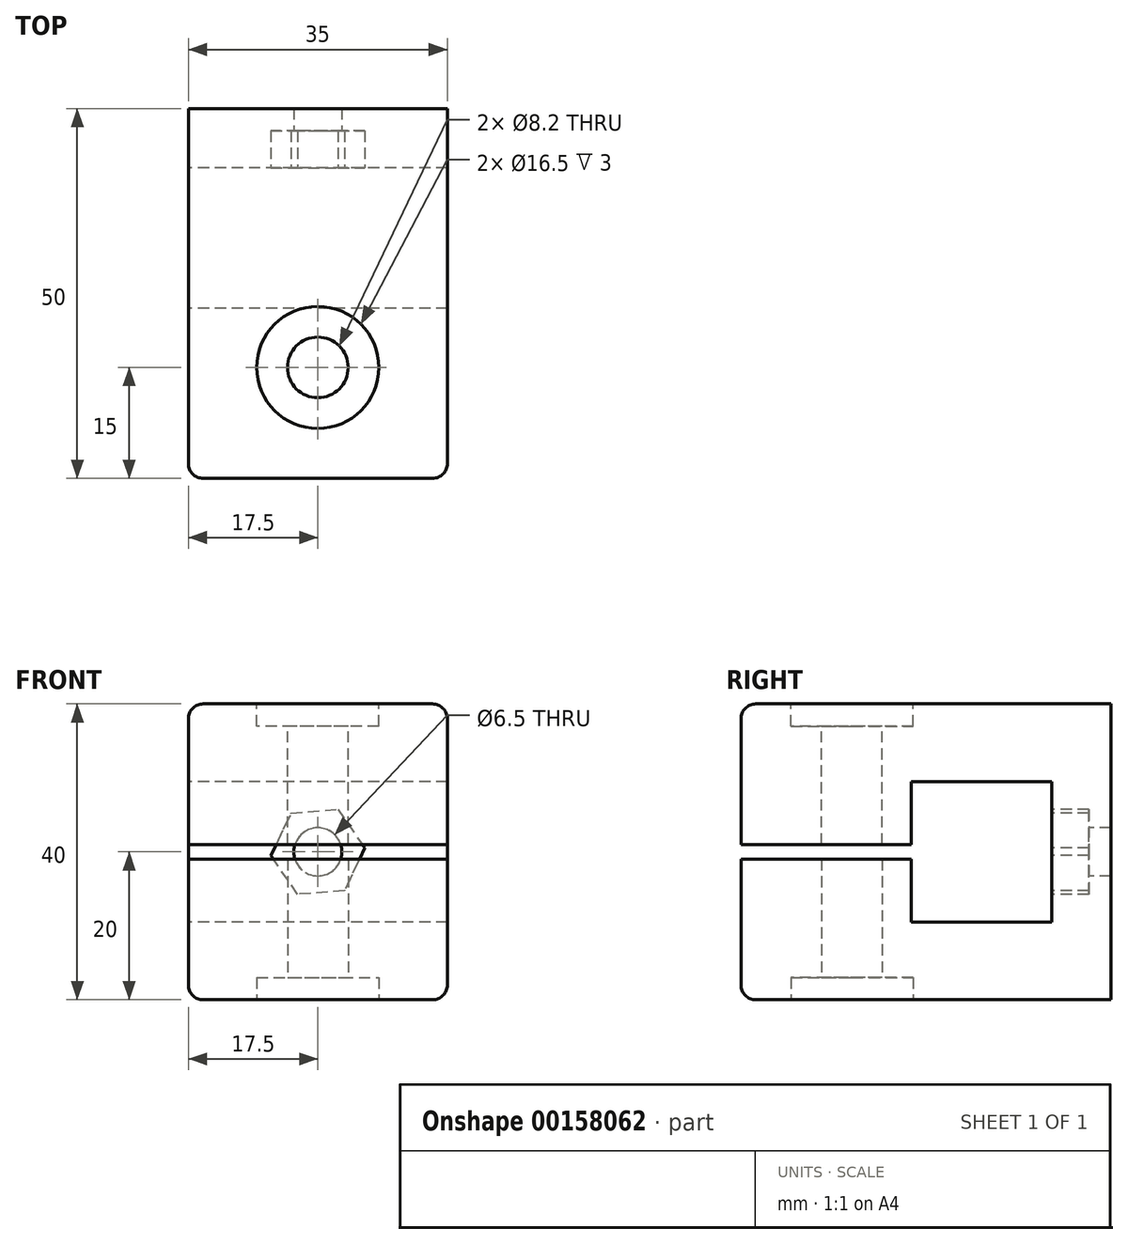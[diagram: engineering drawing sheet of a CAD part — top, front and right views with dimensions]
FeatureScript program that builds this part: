
annotation { "Feature Type Name" : "Feature", "Feature Type Description" : "" }
export const myFeature = defineFeature(function(context is Context, id is Id, definition is map)
    precondition{}
    {
        {
            var Q0;
            Q0=qCreatedBy(makeId("Right.planeOp"),FACE);
            var sketch = newSketch(context, id + "F0", { "sketchPlane" : qUnion([Q0])});
            skLineSegment(sketch, "E0.bottom", {"start": v(9.5, -9.5) * mm, "end": v(-9.5, -9.5) * mm});
            skLineSegment(sketch, "E0.top", {"start": v(9.5, 9.5) * mm, "end": v(-9.5, 9.5) * mm});
            skLineSegment(sketch, "E0.left", {"start": v(9.5, -9.5) * mm, "end": v(9.5, 9.5) * mm});
            skLineSegment(sketch, "E0.right", {"start": v(-9.5, -9.5) * mm, "end": v(-9.5, -1) * mm});
            skPoint(sketch, "E0.middle", {"position": v(0, 0) * mm});
            skLineSegment(sketch, "E1.left", {"start": v(17.5, -20) * mm, "end": v(17.5, 20) * mm});
            skLineSegment(sketch, "E2", {"start": v(17.5, 20) * mm, "end": v(-32.5, 20) * mm});
            skLineSegment(sketch, "E3", {"start": v(-32.5, 20) * mm, "end": v(-32.5, 1) * mm});
            skLineSegment(sketch, "E4", {"start": v(-32.5, -20) * mm, "end": v(17.5, -20) * mm});
            skLineSegment(sketch, "E5", {"start": v(0, 0) * mm, "end": v(0, 29.36) * mm, "construction": true});
            skLineSegment(sketch, "E6", {"start": v(0, 0) * mm, "end": v(0, -29.79) * mm, "construction": true});
            skLineSegment(sketch, "E7", {"start": v(-9.5, -1) * mm, "end": v(-32.5, -1) * mm});
            skLineSegment(sketch, "E8", {"start": v(-32.5, 1) * mm, "end": v(-9.5, 1) * mm});
            skLineSegment(sketch, "E9.trimOffspring", {"start": v(-9.5, 1) * mm, "end": v(-9.5, 9.5) * mm});
            skLineSegment(sketch, "E10.trimOffspring", {"start": v(-32.5, -1) * mm, "end": v(-32.5, -20) * mm});
            skSolve(sketch);
        }
        {
            var Q0;
            Q0 = qSketchRegion(id + "F0", true);
            extrude(context, id + "F1", {"entities" : qUnion([Q0]), "depth" : 35 * mm});
        }
        {
            var Q0;
            Q0=makeQuery(id+"F1.opExtrude","SWEPT_FACE",FACE,{"disambiguationData":[OSD([sQuery(id+"F0.wireOp",EDGE,"E0.left")])]});
            var sketch = newSketch(context, id + "F2", { "sketchPlane" : qUnion([Q0])});
            skPoint(sketch, "E11", {"position": v(17.5, 0) * mm});
            skPoint(sketch, "E11.positionSnap0", {"position": v(17.5, 9.5) * mm});
            skCircle(sketch, "E12.cCircle", {"center": v(17.5, 0) * mm, "radius": 5.5 * mm, "construction": true});
            skLineSegment(sketch, "E12.0", {"start": v(23.83, 0.51) * mm, "end": v(21.1, -5.23) * mm});
            skLineSegment(sketch, "E12.1", {"start": v(21.1, -5.23) * mm, "end": v(14.78, -5.74) * mm});
            skLineSegment(sketch, "E12.2", {"start": v(14.78, -5.74) * mm, "end": v(11.17, -0.51) * mm});
            skLineSegment(sketch, "E12.3", {"start": v(11.17, -0.51) * mm, "end": v(13.9, 5.23) * mm});
            skLineSegment(sketch, "E12.4", {"start": v(13.9, 5.23) * mm, "end": v(20.22, 5.74) * mm});
            skLineSegment(sketch, "E12.5", {"start": v(20.22, 5.74) * mm, "end": v(23.83, 0.51) * mm});
            skPoint(sketch, "E12.0.midPoint", {"position": v(22.47, -2.36) * mm});
            skSolve(sketch);
        }
        {
            var Q0;
            Q0=sQuery(id+"F2.wireOp",VERTEX,"E11");
            var Q1;
            Q1=makeQuery(id+"F1.opExtrude","SWEPT_BODY",BODY,{"disambiguationData":[OSD([sQuery(id+"F0.wireOp",EDGE,"E0.bottom"),sQuery(id+"F0.wireOp",EDGE,"E0.top"),sQuery(id+"F0.wireOp",EDGE,"E0.left"),sQuery(id+"F0.wireOp",EDGE,"E0.right"),sQuery(id+"F0.wireOp",EDGE,"E1.bottom"),sQuery(id+"F0.wireOp",EDGE,"E1.top"),sQuery(id+"F0.wireOp",EDGE,"E1.left"),sQuery(id+"F0.wireOp",EDGE,"E1.right")])]});
            hole(context, id + "F3", {"style" : HoleStyle.C_BORE, "endStyle" : HoleEndStyle.THROUGH, "holeDiameter" : 6.5 * mm, "cBoreDiameter" : 10 * mm, "cBoreDepth" : 4 * mm, "locations" : qUnion([Q0]), "scope" : qUnion([Q1]), "isTappedThrough" : true});
        }
        {
            var Q0;
            Q0=makeQuery(id+"F1.opExtrude","SWEPT_FACE",FACE,{"disambiguationData":[OSD([sQuery(id+"F0.wireOp",EDGE,"E2")])]});
            var sketch = newSketch(context, id + "F4", { "sketchPlane" : qUnion([Q0])});
            skPoint(sketch, "E13", {"position": v(17.5, -17.5) * mm});
            skPoint(sketch, "E13.positionSnap1", {"position": v(17.5, -32.5) * mm});
            skSolve(sketch);
        }
        {
            var Q0;
            Q0=sQuery(id+"F4.wireOp",VERTEX,"E13");
            var Q1;
            Q1=makeQuery(id+"F1.opExtrude","SWEPT_BODY",BODY,{"disambiguationData":[OSD([sQuery(id+"F0.wireOp",EDGE,"E0.bottom"),sQuery(id+"F0.wireOp",EDGE,"E0.top"),sQuery(id+"F0.wireOp",EDGE,"E0.left"),sQuery(id+"F0.wireOp",EDGE,"E0.right"),sQuery(id+"F0.wireOp",EDGE,"E1.bottom"),sQuery(id+"F0.wireOp",EDGE,"E1.top"),sQuery(id+"F0.wireOp",EDGE,"E1.left"),sQuery(id+"F0.wireOp",EDGE,"E1.right")])]});
            hole(context, id + "F5", {"style" : HoleStyle.C_BORE, "endStyle" : HoleEndStyle.BLIND, "holeDiameter" : 8.2 * mm, "cBoreDiameter" : 16.5 * mm, "cBoreDepth" : 3 * mm, "holeDepth" : 20 * mm, "locations" : qUnion([Q0]), "scope" : qUnion([Q1])});
        }
        {
            var Q0;
            Q0=makeQuery(id+"F1.opExtrude","SWEPT_FACE",FACE,{"disambiguationData":[OSD([sQuery(id+"F0.wireOp",EDGE,"E4")])]});
            var sketch = newSketch(context, id + "F6", { "sketchPlane" : qUnion([Q0])});
            skPoint(sketch, "E14", {"position": v(17.5, 17.5) * mm});
            skPoint(sketch, "E14.positionSnap1", {"position": v(17.5, 32.5) * mm});
            skSolve(sketch);
        }
        {
            var Q0;
            Q0=sQuery(id+"F6.wireOp",VERTEX,"E14");
            var Q1;
            Q1=makeQuery(id+"F1.opExtrude","SWEPT_BODY",BODY,{"disambiguationData":[OSD([sQuery(id+"F0.wireOp",EDGE,"E0.bottom"),sQuery(id+"F0.wireOp",EDGE,"E0.top"),sQuery(id+"F0.wireOp",EDGE,"E0.left"),sQuery(id+"F0.wireOp",EDGE,"E0.right"),sQuery(id+"F0.wireOp",EDGE,"E1.bottom"),sQuery(id+"F0.wireOp",EDGE,"E1.top"),sQuery(id+"F0.wireOp",EDGE,"E1.left"),sQuery(id+"F0.wireOp",EDGE,"E1.right")])]});
            hole(context, id + "F7", {"style" : HoleStyle.C_BORE, "endStyle" : HoleEndStyle.BLIND, "holeDiameter" : 8.2 * mm, "cBoreDiameter" : 16.5 * mm, "cBoreDepth" : 3 * mm, "holeDepth" : 20 * mm, "locations" : qUnion([Q0]), "scope" : qUnion([Q1])});
        }
        {
            var Q0;
            Q0=makeQuery(id+"F1.opExtrude","SWEPT_EDGE",EDGE,{"disambiguationData":[OSD([sQuery(id+"F0.wireOp",EDGE,"E2"),sQuery(id+"F0.wireOp",EDGE,"E3")])]});
            var Q1;
            Q1=makeQuery(id+"F1.opExtrude","CAP_EDGE",EDGE,{"disambiguationData":[OSD([sQuery(id+"F0.wireOp",EDGE,"E2")])],"isStart":true});
            var Q2;
            Q2=makeQuery(id+"F1.opExtrude","CAP_EDGE",EDGE,{"disambiguationData":[OSD([sQuery(id+"F0.wireOp",EDGE,"E2")])],"isStart":false});
            var Q3;
            Q3=makeQuery(id+"F1.opExtrude","CAP_EDGE",EDGE,{"disambiguationData":[OSD([sQuery(id+"F0.wireOp",EDGE,"E4")])],"isStart":true});
            var Q4;
            Q4=makeQuery(id+"F1.opExtrude","SWEPT_EDGE",EDGE,{"disambiguationData":[OSD([sQuery(id+"F0.wireOp",EDGE,"E4"),sQuery(id+"F0.wireOp",EDGE,"E10.trimOffspring")])]});
            var Q5;
            Q5=makeQuery(id+"F1.opExtrude","CAP_EDGE",EDGE,{"disambiguationData":[OSD([sQuery(id+"F0.wireOp",EDGE,"E4")])],"isStart":false});
            var Q6;
            Q6=makeQuery(id+"F1.opExtrude","CAP_EDGE",EDGE,{"disambiguationData":[OSD([sQuery(id+"F0.wireOp",EDGE,"E3")])],"isStart":true});
            var Q7;
            Q7=makeQuery(id+"F1.opExtrude","CAP_EDGE",EDGE,{"disambiguationData":[OSD([sQuery(id+"F0.wireOp",EDGE,"E10.trimOffspring")])],"isStart":true});
            var Q8;
            Q8=makeQuery(id+"F1.opExtrude","CAP_EDGE",EDGE,{"disambiguationData":[OSD([sQuery(id+"F0.wireOp",EDGE,"E10.trimOffspring")])],"isStart":false});
            var Q9;
            Q9=makeQuery(id+"F1.opExtrude","CAP_EDGE",EDGE,{"disambiguationData":[OSD([sQuery(id+"F0.wireOp",EDGE,"E3")])],"isStart":false});
            fillet(context, id + "F8", {"entities" : qUnion([Q0, Q1, Q2, Q3, Q4, Q5, Q6, Q7, Q8, Q9]), "radius" : 2 * mm, "tangentPropagation" : true, "allowEdgeOverflow" : false});
        }
        {
            var Q0;
            Q0 = qSketchRegion(id + "F2", true);
            extrude(context, id + "F9", {"entities" : qUnion([Q0]), "operationType" : NewBodyOperationType.REMOVE, "oppositeDirection" : true, "depth" : 5 * mm});
        }
    });
